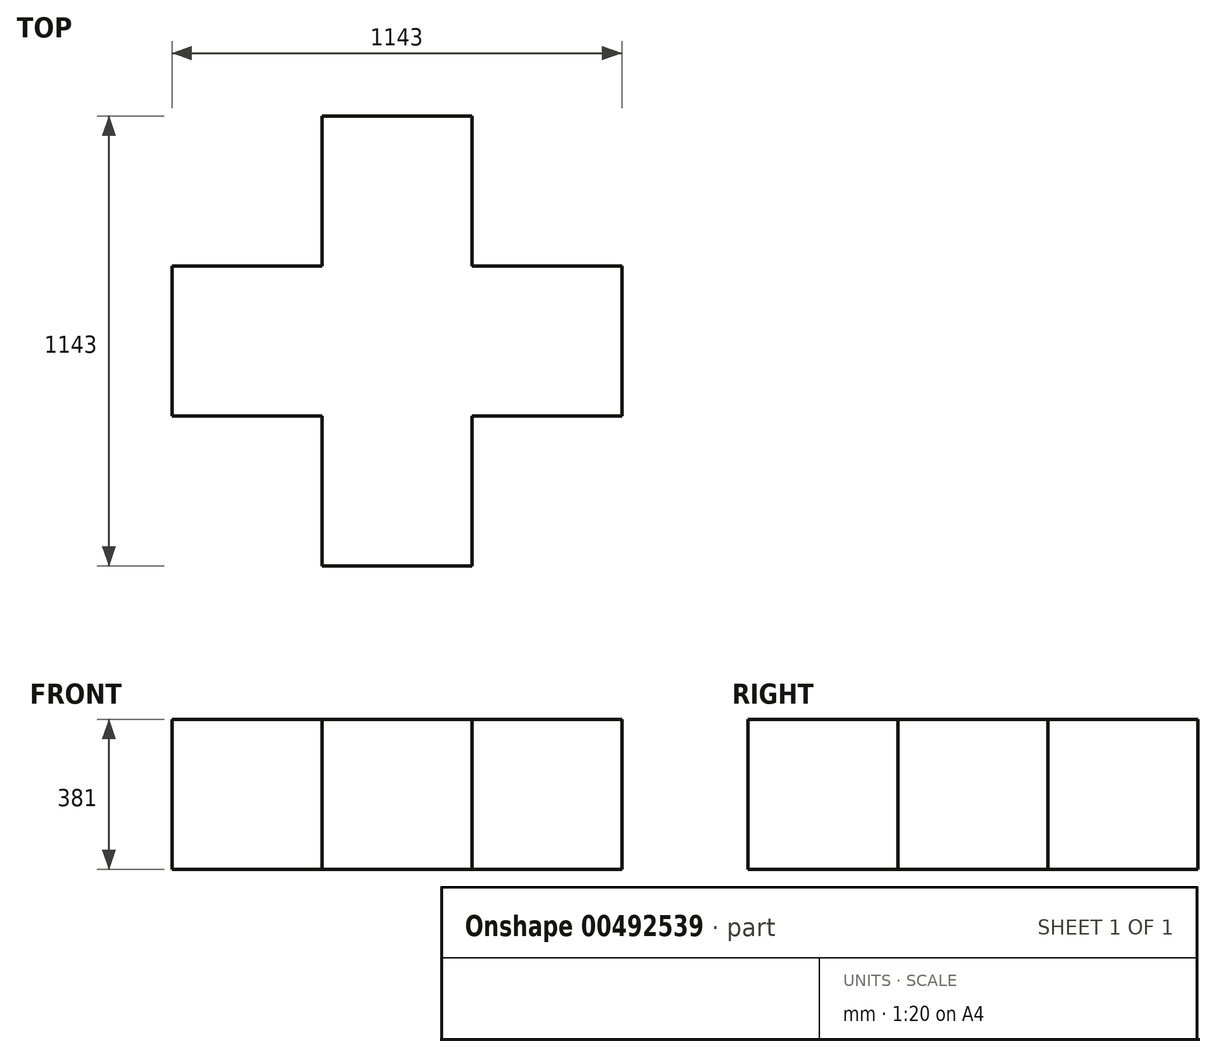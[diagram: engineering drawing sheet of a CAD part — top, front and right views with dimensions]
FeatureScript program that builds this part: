
annotation { "Feature Type Name" : "Feature", "Feature Type Description" : "" }
export const myFeature = defineFeature(function(context is Context, id is Id, definition is map)
    precondition{}
    {
        {
            var Q0;
            Q0=qCreatedBy(makeId("Top.planeOp"),FACE);
            var sketch = newSketch(context, id + "F0", { "sketchPlane" : qUnion([Q0])});
            skLineSegment(sketch, "E0.bottom", {"start": v(571.5, 571.5) * mm, "end": v(-571.5, 571.5) * mm});
            skLineSegment(sketch, "E0.top", {"start": v(571.5, -571.5) * mm, "end": v(-571.5, -571.5) * mm});
            skLineSegment(sketch, "E0.left", {"start": v(571.5, 571.5) * mm, "end": v(571.5, -571.5) * mm});
            skLineSegment(sketch, "E0.right", {"start": v(-571.5, 571.5) * mm, "end": v(-571.5, -571.5) * mm});
            skPoint(sketch, "E0.middle", {"position": v(0, 0) * mm});
            skLineSegment(sketch, "E1", {"start": v(-571.5, 190.5) * mm, "end": v(-190.5, 190.5) * mm});
            skLineSegment(sketch, "E2", {"start": v(-190.5, 190.5) * mm, "end": v(-190.5, 571.5) * mm});
            skLineSegment(sketch, "E3", {"start": v(0, 571.5) * mm, "end": v(0, -571.5) * mm, "construction": true});
            skLineSegment(sketch, "E4", {"start": v(-571.5, 0) * mm, "end": v(571.5, 0) * mm, "construction": true});
            skLineSegment(sketch, "E5.MirrorCS", {"start": v(190.5, 190.5) * mm, "end": v(190.5, 571.5) * mm});
            skLineSegment(sketch, "E6.MirrorCS", {"start": v(571.5, 190.5) * mm, "end": v(190.5, 190.5) * mm});
            skLineSegment(sketch, "E7.MirrorCS", {"start": v(-571.5, -190.5) * mm, "end": v(-190.5, -190.5) * mm});
            skLineSegment(sketch, "E8.MirrorCS", {"start": v(-190.5, -190.5) * mm, "end": v(-190.5, -571.5) * mm});
            skLineSegment(sketch, "E9.MirrorCS", {"start": v(190.5, -190.5) * mm, "end": v(190.5, -571.5) * mm});
            skLineSegment(sketch, "E10.MirrorCS", {"start": v(571.5, -190.5) * mm, "end": v(190.5, -190.5) * mm});
            skSolve(sketch);
        }
        {
            var Q0;
            {var subQ4=sQuery(id+"F0.wireOp",EDGE,"E1");Q0=makeQuery(id+"F0.imprint","IMPRINT",FACE,{"disambiguationData":[TD([[makeQuery(id+"F0.imprint","IMPRINT",EDGE,{"derivedFrom":subQ4}),-1.0]])]});}
            extrude(context, id + "F1", {"entities" : qUnion([Q0]), "depth" : 381 * mm});
        }
    });
